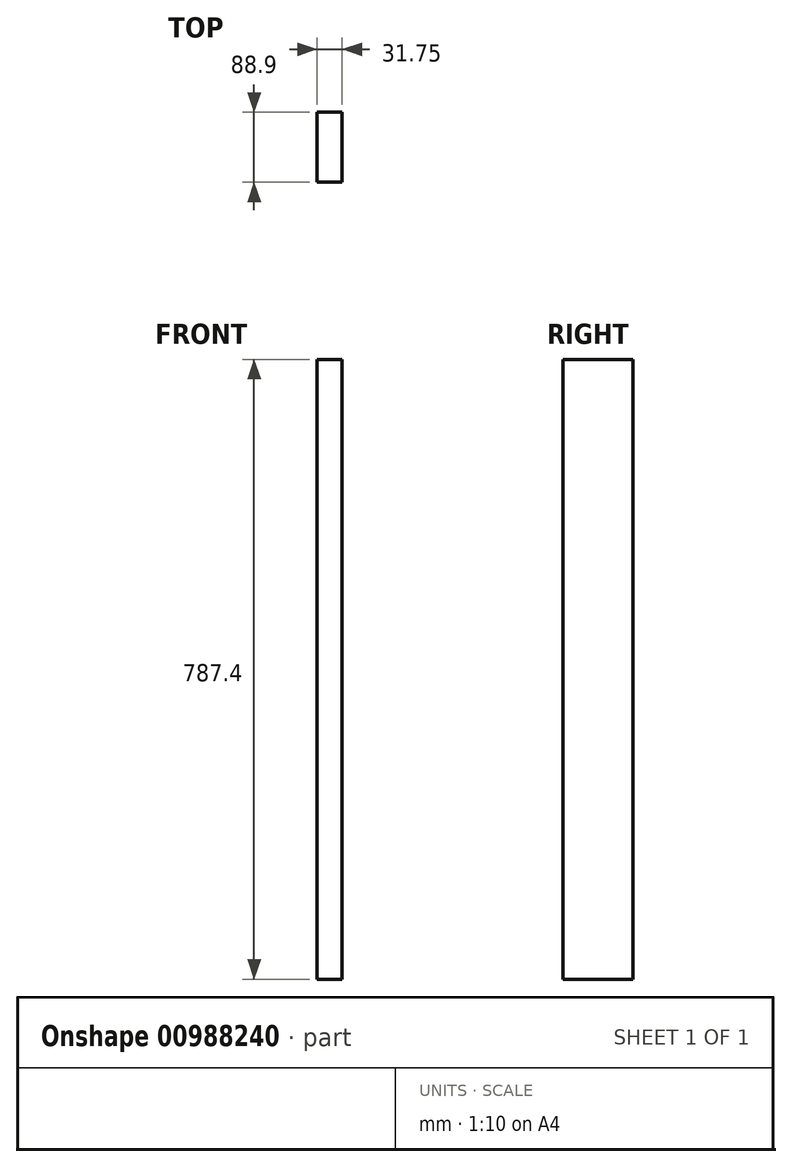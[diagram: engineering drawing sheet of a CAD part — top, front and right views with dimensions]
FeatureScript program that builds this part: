
annotation { "Feature Type Name" : "Feature", "Feature Type Description" : "" }
export const myFeature = defineFeature(function(context is Context, id is Id, definition is map)
    precondition{}
    {
        {
            var Q0;
            Q0=qCreatedBy(makeId("Right.planeOp"),FACE);
            var sketch = newSketch(context, id + "F0", { "sketchPlane" : qUnion([Q0])});
            skLineSegment(sketch, "E0.bottom", {"start": v(0, 0) * mm, "end": v(88.9, 0) * mm});
            skLineSegment(sketch, "E0.left", {"start": v(0, 0) * mm, "end": v(0, 787.4) * mm});
            skLineSegment(sketch, "E0.right", {"start": v(88.9, 0) * mm, "end": v(88.9, 787.4) * mm});
            skLineSegment(sketch, "E1", {"start": v(88.9, 787.4) * mm, "end": v(0, 787.4) * mm});
            skSolve(sketch);
        }
        {
            var Q0;
            Q0 = qSketchRegion(id + "F0", true);
            extrude(context, id + "F1", {"entities" : qUnion([Q0]), "depth" : 31.75 * mm, "offsetDistance" : 25.4 * mm});
        }
    });
